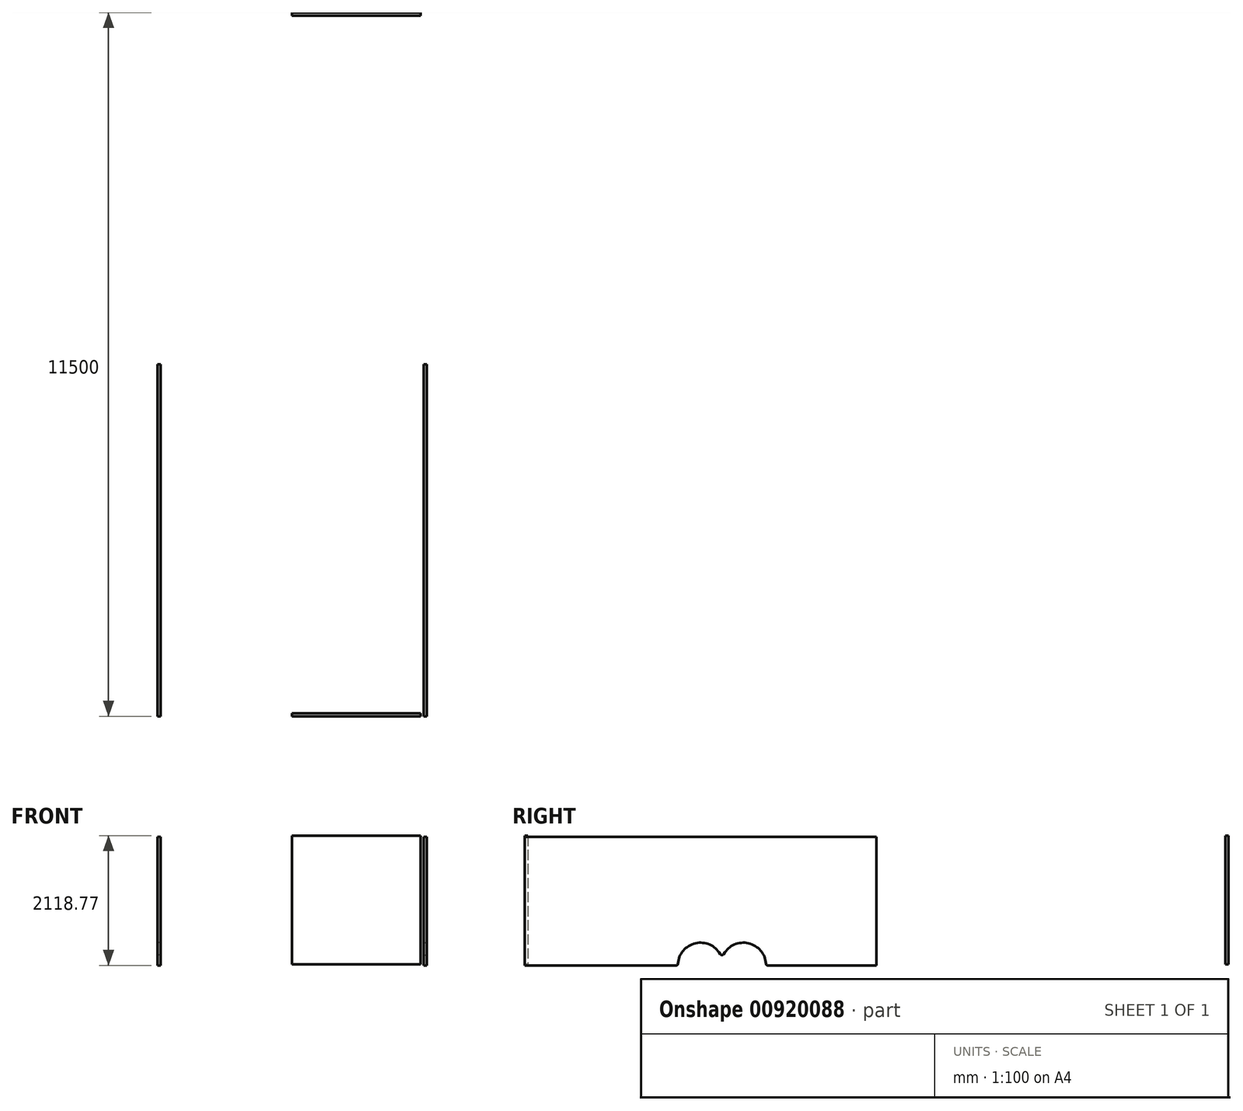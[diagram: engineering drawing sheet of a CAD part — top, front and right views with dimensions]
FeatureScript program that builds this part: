
annotation { "Feature Type Name" : "Feature", "Feature Type Description" : "" }
export const myFeature = defineFeature(function(context is Context, id is Id, definition is map)
    precondition{}
    {
        {
            var Q0;
            Q0=qCreatedBy(makeId("Right.planeOp"),FACE);
            var sketch = newSketch(context, id + "F0", { "sketchPlane" : qUnion([Q0])});
            skLineSegment(sketch, "E0", {"start": v(2865.34, -1465.72) * mm, "end": v(1086.3, -1465.72) * mm});
            skLineSegment(sketch, "E1", {"start": v(-2884.66, -1465.72) * mm, "end": v(-2884.66, 634.28) * mm});
            skLineSegment(sketch, "E2", {"start": v(-2884.66, 634.28) * mm, "end": v(2865.34, 634.28) * mm});
            skLineSegment(sketch, "E3", {"start": v(2865.34, 634.28) * mm, "end": v(2865.34, -1465.72) * mm});
            skArc(sketch, "E4", {"start": v(311.02, -1281.09) * mm, "mid": v(-93.38, -1105.28) * mm, "end": v(-378.88, -1441.34) * mm});
            skArc(sketch, "E5", {"start": v(1060.27, -1441.34) * mm, "mid": v(774.76, -1105.28) * mm, "end": v(370.36, -1281.09) * mm});
            skArc(sketch, "E6", {"start": v(311.02, -1281.09) * mm, "mid": v(340.7, -1298.24) * mm, "end": v(370.36, -1281.09) * mm});
            skArc(sketch, "E7", {"start": v(-404.93, -1465.72) * mm, "mid": v(-387.1, -1458.67) * mm, "end": v(-378.88, -1441.34) * mm});
            skArc(sketch, "E8", {"start": v(1060.27, -1441.34) * mm, "mid": v(1068.47, -1458.67) * mm, "end": v(1086.3, -1465.72) * mm});
            skLineSegment(sketch, "E9.trimOffspring", {"start": v(-404.93, -1465.72) * mm, "end": v(-2884.66, -1465.72) * mm});
            skSolve(sketch);
        }
        {
            var Q0;
            Q0=makeQuery(id+"F0.imprint","IMPRINT",FACE,{"disambiguationData":[TD([[makeQuery(id+"F0.imprint","IMPRINT",EDGE,{"derivedFrom":sQuery(id+"F0.wireOp",EDGE,"E0")}),-1.0]])]});
            extrude(context, id + "F1", {"entities" : qUnion([Q0]), "oppositeDirection" : true, "depth" : 50 * mm, "offsetDistance" : 25 * mm});
        }
        {
            var Q0;
            Q0=makeQuery(id+"F1.opExtrude","SWEPT_FACE",FACE,{"disambiguationData":[OSD([sQuery(id+"F0.wireOp",EDGE,"E1")])]});
            var sketch = newSketch(context, id + "F2", { "sketchPlane" : qUnion([Q0])});
            skLineSegment(sketch, "E10.bottom", {"start": v(-100, 653.05) * mm, "end": v(-2200, 653.05) * mm});
            skLineSegment(sketch, "E10.top", {"start": v(-100, -1446.95) * mm, "end": v(-2200, -1446.95) * mm});
            skLineSegment(sketch, "E10.left", {"start": v(-100, 653.05) * mm, "end": v(-100, -1446.95) * mm});
            skLineSegment(sketch, "E10.right", {"start": v(-2200, 653.05) * mm, "end": v(-2200, -1446.95) * mm});
            skSolve(sketch);
        }
        {
            var Q0;
            Q0=makeQuery(id+"F2.imprint","IMPRINT",FACE,{"disambiguationData":[TD([[makeQuery(id+"F2.imprint","IMPRINT",EDGE,{"derivedFrom":sQuery(id+"F2.wireOp",EDGE,"E10.bottom")}),1.0]])]});
            extrude(context, id + "F3", {"entities" : qUnion([Q0]), "oppositeDirection" : true, "depth" : 50 * mm, "offsetDistance" : 25 * mm});
        }
        {
            var Q0;
            Q0=makeQuery(id+"F1.opExtrude","SWEPT_BODY",BODY,{"disambiguationData":[OSD([sQuery(id+"F0.wireOp",EDGE,"E0"),sQuery(id+"F0.wireOp",EDGE,"E1"),sQuery(id+"F0.wireOp",EDGE,"E2"),sQuery(id+"F0.wireOp",EDGE,"E3"),sQuery(id+"F0.wireOp",EDGE,"E4"),sQuery(id+"F0.wireOp",EDGE,"E5"),sQuery(id+"F0.wireOp",EDGE,"E6"),sQuery(id+"F0.wireOp",EDGE,"E7"),sQuery(id+"F0.wireOp",EDGE,"E8"),sQuery(id+"F0.wireOp",EDGE,"E9.trimOffspring")])]});
            var Q1;
            Q1=makeQuery(id+"F3.opExtrude","SWEPT_FACE",FACE,{"disambiguationData":[OSD([sQuery(id+"F2.wireOp",EDGE,"E10.right")])]});
            mirror(context, id + "F4", {"operationType" : NewBodyOperationType.ADD, "entities" : qUnion([Q0]), "mirrorPlane" : qUnion([Q1])});
        }
        {
            var Q0;
            Q0=makeQuery(id+"F3.opExtrude","SWEPT_BODY",BODY,{"disambiguationData":[OSD([sQuery(id+"F2.wireOp",EDGE,"E10.bottom"),sQuery(id+"F2.wireOp",EDGE,"E10.top"),sQuery(id+"F2.wireOp",EDGE,"E10.left"),sQuery(id+"F2.wireOp",EDGE,"E10.right")])]});
            var Q1;
            Q1=makeQuery(id+"F1.opExtrude","SWEPT_FACE",FACE,{"disambiguationData":[OSD([sQuery(id+"F0.wireOp",EDGE,"E3")])]});
            mirror(context, id + "F5", {"entities" : qUnion([Q0]), "mirrorPlane" : qUnion([Q1])});
        }
    });
